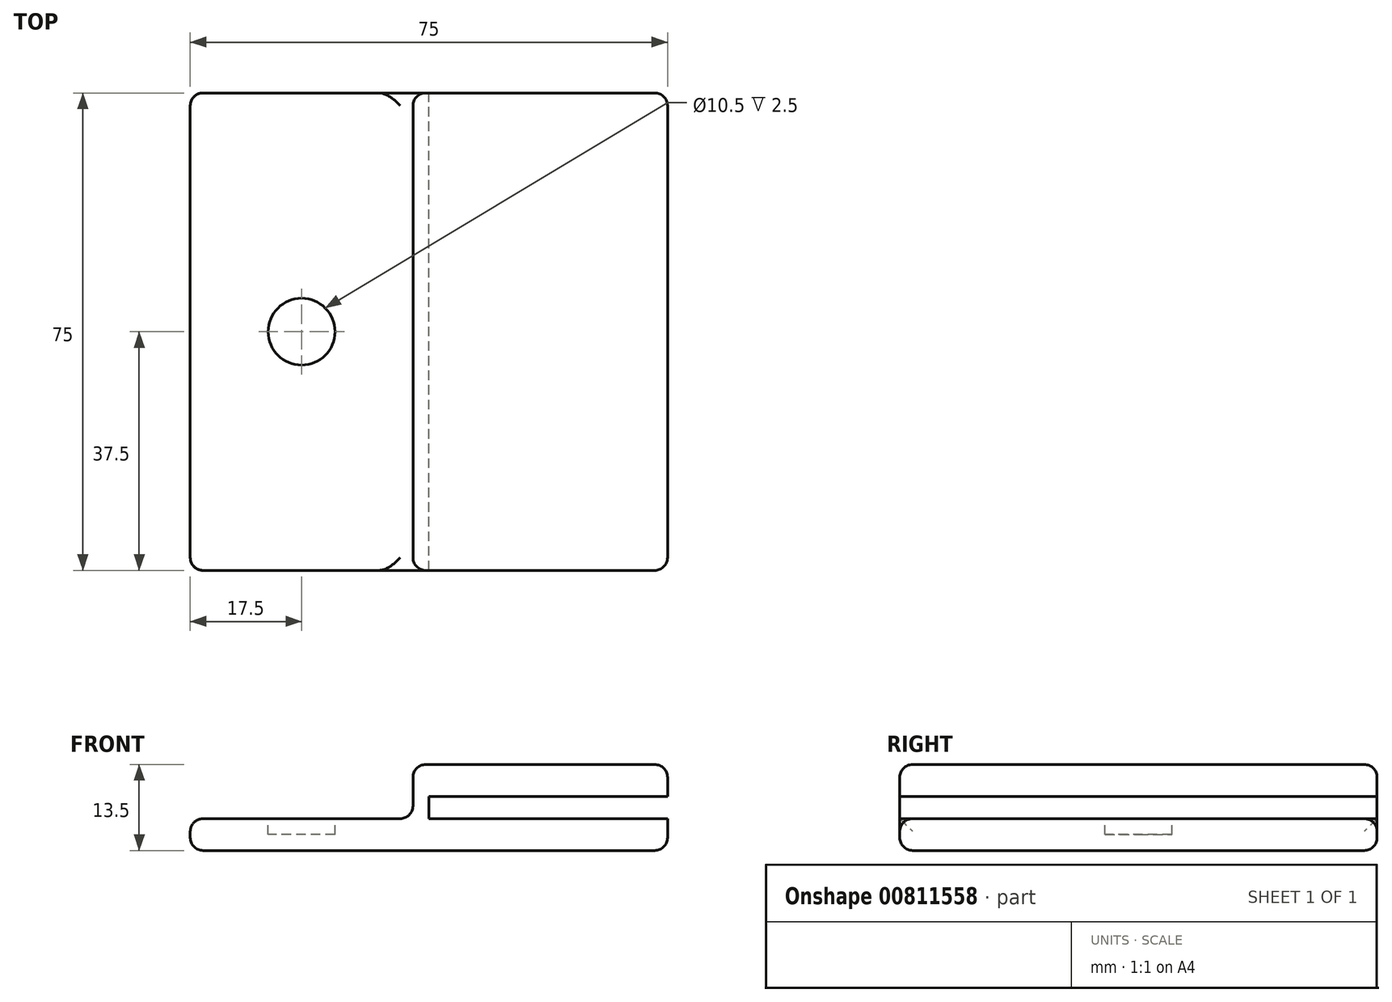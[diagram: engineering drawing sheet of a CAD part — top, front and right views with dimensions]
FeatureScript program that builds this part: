
annotation { "Feature Type Name" : "Feature", "Feature Type Description" : "" }
export const myFeature = defineFeature(function(context is Context, id is Id, definition is map)
    precondition{}
    {
        {
            var Q0;
            Q0=qCreatedBy(makeId("Top.planeOp"),FACE);
            var sketch = newSketch(context, id + "F0", { "sketchPlane" : qUnion([Q0])});
            skLineSegment(sketch, "E0.bottom", {"start": v(37.5, -37.5) * mm, "end": v(-37.5, -37.5) * mm});
            skLineSegment(sketch, "E0.top", {"start": v(37.5, 37.5) * mm, "end": v(-37.5, 37.5) * mm});
            skLineSegment(sketch, "E0.left", {"start": v(37.5, -37.5) * mm, "end": v(37.5, 37.5) * mm});
            skLineSegment(sketch, "E0.right", {"start": v(-37.5, -37.5) * mm, "end": v(-37.5, 37.5) * mm});
            skPoint(sketch, "E0.middle", {"position": v(0, 0) * mm});
            skSolve(sketch);
        }
        {
            var Q0;
            Q0=qSketchRegion(id+"F0",true);
            extrude(context, id + "F1", {"entities" : qUnion([Q0]), "depth" : 5 * mm, "offsetDistance" : 25 * mm});
        }
        {
            var Q0;
            Q0=makeQuery(id+"F1.opExtrude","CAP_FACE",FACE,{"disambiguationData":[OSD([sQuery(id+"F0.wireOp",EDGE,"E0.bottom"),sQuery(id+"F0.wireOp",EDGE,"E0.top"),sQuery(id+"F0.wireOp",EDGE,"E0.left"),sQuery(id+"F0.wireOp",EDGE,"E0.right")])],"isStart":false});
            var sketch = newSketch(context, id + "F2", { "sketchPlane" : qUnion([Q0])});
            skLineSegment(sketch, "E1.bottom", {"start": v(-2.5, 37.5) * mm, "end": v(37.5, 37.5) * mm});
            skLineSegment(sketch, "E1.top", {"start": v(-2.5, -37.5) * mm, "end": v(37.5, -37.5) * mm});
            skLineSegment(sketch, "E1.left", {"start": v(-2.5, 37.5) * mm, "end": v(-2.5, -37.5) * mm});
            skLineSegment(sketch, "E1.right", {"start": v(37.5, 37.5) * mm, "end": v(37.5, -37.5) * mm});
            skSolve(sketch);
        }
        {
            var Q0;
            Q0=qSketchRegion(id+"F2",true);
            extrude(context, id + "F3", {"entities" : qUnion([Q0]), "operationType" : NewBodyOperationType.ADD, "depth" : 8.5 * mm, "offsetDistance" : 25 * mm});
        }
        {
            var Q0;
            Q0=makeQuery(id+"F3.boolean.opBoolean","MERGE",FACE,{"derivedFrom":[makeQuery(id+"F1.opExtrude","SWEPT_FACE",FACE,{"disambiguationData":[OSD([sQuery(id+"F0.wireOp",EDGE,"E0.left")])]}),makeQuery(id+"F3.opExtrude","SWEPT_FACE",FACE,{"disambiguationData":[OSD([sQuery(id+"F2.wireOp",EDGE,"E1.right")])]})]});
            var sketch = newSketch(context, id + "F4", { "sketchPlane" : qUnion([Q0])});
            skLineSegment(sketch, "E2.bottom", {"start": v(37.5, 8.5) * mm, "end": v(-37.5, 8.5) * mm});
            skLineSegment(sketch, "E2.top", {"start": v(37.5, 5) * mm, "end": v(-37.5, 5) * mm});
            skLineSegment(sketch, "E2.left", {"start": v(37.5, 8.5) * mm, "end": v(37.5, 5) * mm});
            skLineSegment(sketch, "E2.right", {"start": v(-37.5, 8.5) * mm, "end": v(-37.5, 5) * mm});
            skSolve(sketch);
        }
        {
            var Q0;
            Q0=qSketchRegion(id+"F4",true);
            var Q1;
            Q1=makeQuery(id+"F3.opExtrude","SWEPT_FACE",FACE,{"disambiguationData":[OSD([sQuery(id+"F2.wireOp",EDGE,"E1.left")])]});
            extrude(context, id + "F5", {"entities" : qUnion([Q0]), "operationType" : NewBodyOperationType.REMOVE, "endBound" : BoundingType.UP_TO_SURFACE, "oppositeDirection" : true, "depth" : 25 * mm, "endBoundEntityFace" : qUnion([Q1]), "hasOffset" : true, "offsetDistance" : 2.5 * mm});
        }
        {
            var Q0;
            Q0=makeQuery(id+"F1.opExtrude","CAP_FACE",FACE,{"disambiguationData":[OSD([sQuery(id+"F0.wireOp",EDGE,"E0.bottom"),sQuery(id+"F0.wireOp",EDGE,"E0.top"),sQuery(id+"F0.wireOp",EDGE,"E0.left"),sQuery(id+"F0.wireOp",EDGE,"E0.right")])],"isStart":false});
            var sketch = newSketch(context, id + "F6", { "sketchPlane" : qUnion([Q0])});
            skLineSegment(sketch, "E3", {"start": v(-20, 37.5) * mm, "end": v(-20, -37.5) * mm, "construction": true});
            skLineSegment(sketch, "E4", {"start": v(-37.5, 0) * mm, "end": v(-2.5, 0) * mm, "construction": true});
            skCircle(sketch, "E5", {"center": v(-20, 0) * mm, "radius": 5.25 * mm});
            skSolve(sketch);
        }
        {
            var Q0;
            Q0=qSketchRegion(id+"F6",true);
            extrude(context, id + "F7", {"entities" : qUnion([Q0]), "operationType" : NewBodyOperationType.REMOVE, "oppositeDirection" : true, "depth" : 2.5 * mm, "offsetDistance" : 25 * mm});
        }
        {
            var Q0;
            Q0=makeQuery(id+"F3.opExtrude","CAP_FACE",FACE,{"disambiguationData":[OSD([sQuery(id+"F2.wireOp",EDGE,"E1.bottom"),sQuery(id+"F2.wireOp",EDGE,"E1.top"),sQuery(id+"F2.wireOp",EDGE,"E1.left"),sQuery(id+"F2.wireOp",EDGE,"E1.right")])],"isStart":false});
            var Q1;
            Q1=makeQuery(id+"F3.opExtrude","SWEPT_FACE",FACE,{"disambiguationData":[OSD([sQuery(id+"F2.wireOp",EDGE,"E1.left")])]});
            var Q2;
            Q2=makeQuery(id+"F1.opExtrude","SWEPT_FACE",FACE,{"disambiguationData":[OSD([sQuery(id+"F0.wireOp",EDGE,"E0.right")])]});
            var Q3;
            Q3=makeQuery(id+"F1.opExtrude","CAP_FACE",FACE,{"disambiguationData":[OSD([sQuery(id+"F0.wireOp",EDGE,"E0.bottom"),sQuery(id+"F0.wireOp",EDGE,"E0.top"),sQuery(id+"F0.wireOp",EDGE,"E0.left"),sQuery(id+"F0.wireOp",EDGE,"E0.right")])],"isStart":true});
            var Q4;
            {var subQ0=sQuery(id+"F2.wireOp",EDGE,"E1.top");var subQ1=sQuery(id+"F0.wireOp",EDGE,"E0.left");var subQ2=sQuery(id+"F2.wireOp",EDGE,"E1.right");var subQ3=sQuery(id+"F0.wireOp",EDGE,"E0.bottom");Q4=makeQuery(id+"F5.boolean.opBoolean","SPLIT",EDGE,{"disambiguationData":[TD([makeQuery(id+"F5.opExtrude","SWEPT_FACE",FACE,{"disambiguationData":[OSD([sQuery(id+"F4.wireOp",EDGE,"E2.bottom")])]})])],"derivedFrom":makeQuery(id+"F3.boolean.opBoolean","MERGE",EDGE,{"derivedFrom":[makeQuery(id+"F1.opExtrude","SWEPT_EDGE",EDGE,{"disambiguationData":[OSD([subQ3,subQ1])]}),makeQuery(id+"F3.opExtrude","SWEPT_EDGE",EDGE,{"disambiguationData":[OSD([subQ0,subQ2])]})]})});}
            var Q5;
            {var subQ0=sQuery(id+"F0.wireOp",EDGE,"E0.left");var subQ1=sQuery(id+"F2.wireOp",EDGE,"E1.top");var subQ2=sQuery(id+"F0.wireOp",EDGE,"E0.bottom");var subQ3=sQuery(id+"F2.wireOp",EDGE,"E1.right");Q5=makeQuery(id+"F5.boolean.opBoolean","SPLIT",EDGE,{"disambiguationData":[TD([makeQuery(id+"F5.opExtrude","SWEPT_FACE",FACE,{"disambiguationData":[OSD([sQuery(id+"F4.wireOp",EDGE,"E2.top")])]})])],"derivedFrom":makeQuery(id+"F3.boolean.opBoolean","MERGE",EDGE,{"derivedFrom":[makeQuery(id+"F1.opExtrude","SWEPT_EDGE",EDGE,{"disambiguationData":[OSD([subQ2,subQ0])]}),makeQuery(id+"F3.opExtrude","SWEPT_EDGE",EDGE,{"disambiguationData":[OSD([subQ1,subQ3])]})]})});}
            var Q6;
            {var subQ0=sQuery(id+"F2.wireOp",EDGE,"E1.right");var subQ1=sQuery(id+"F2.wireOp",EDGE,"E1.bottom");var subQ2=sQuery(id+"F0.wireOp",EDGE,"E0.top");var subQ3=sQuery(id+"F0.wireOp",EDGE,"E0.left");Q6=makeQuery(id+"F5.boolean.opBoolean","SPLIT",EDGE,{"disambiguationData":[TD([makeQuery(id+"F5.opExtrude","SWEPT_FACE",FACE,{"disambiguationData":[OSD([sQuery(id+"F4.wireOp",EDGE,"E2.bottom")])]})])],"derivedFrom":makeQuery(id+"F3.boolean.opBoolean","MERGE",EDGE,{"derivedFrom":[makeQuery(id+"F1.opExtrude","SWEPT_EDGE",EDGE,{"disambiguationData":[OSD([subQ2,subQ3])]}),makeQuery(id+"F3.opExtrude","SWEPT_EDGE",EDGE,{"disambiguationData":[OSD([subQ1,subQ0])]})]})});}
            var Q7;
            {var subQ0=sQuery(id+"F0.wireOp",EDGE,"E0.left");var subQ1=sQuery(id+"F2.wireOp",EDGE,"E1.bottom");var subQ2=sQuery(id+"F0.wireOp",EDGE,"E0.top");var subQ3=sQuery(id+"F2.wireOp",EDGE,"E1.right");Q7=makeQuery(id+"F5.boolean.opBoolean","SPLIT",EDGE,{"disambiguationData":[TD([makeQuery(id+"F5.opExtrude","SWEPT_FACE",FACE,{"disambiguationData":[OSD([sQuery(id+"F4.wireOp",EDGE,"E2.top")])]})])],"derivedFrom":makeQuery(id+"F3.boolean.opBoolean","MERGE",EDGE,{"derivedFrom":[makeQuery(id+"F1.opExtrude","SWEPT_EDGE",EDGE,{"disambiguationData":[OSD([subQ2,subQ0])]}),makeQuery(id+"F3.opExtrude","SWEPT_EDGE",EDGE,{"disambiguationData":[OSD([subQ1,subQ3])]})]})});}
            fillet(context, id + "F8", {"entities" : qUnion([Q0, Q1, Q2, Q3, Q4, Q5, Q6, Q7]), "radius" : 2 * mm, "tangentPropagation" : true, "allowEdgeOverflow" : false});
        }
    });
